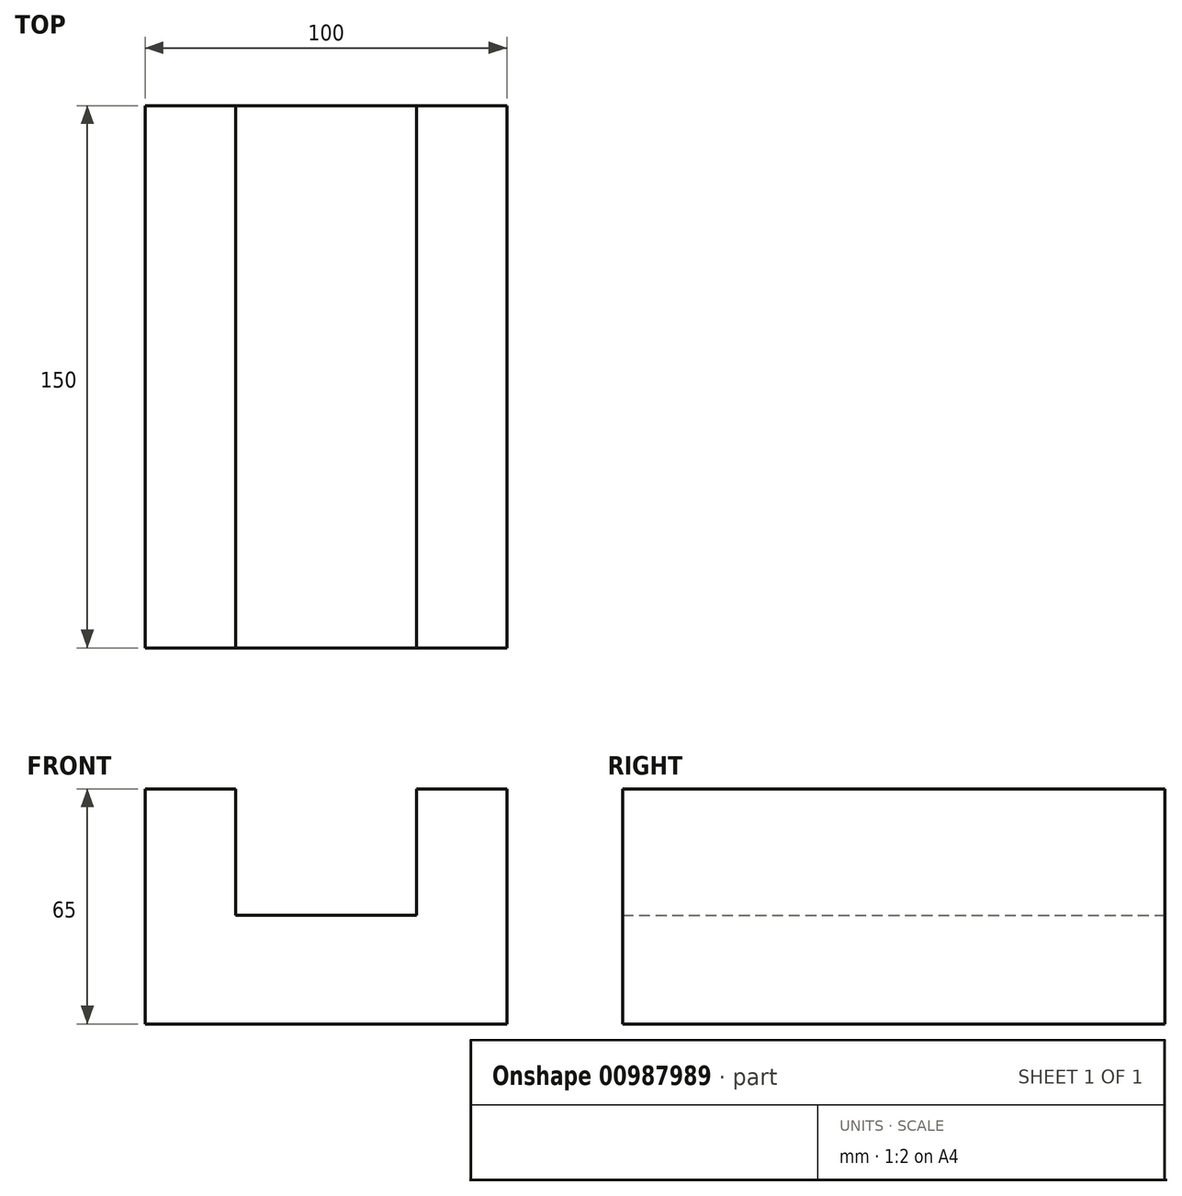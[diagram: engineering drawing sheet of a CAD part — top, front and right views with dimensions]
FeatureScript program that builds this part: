
annotation { "Feature Type Name" : "Feature", "Feature Type Description" : "" }
export const myFeature = defineFeature(function(context is Context, id is Id, definition is map)
    precondition{}
    {
        {
            var Q0;
            Q0=qCreatedBy(makeId("Front.planeOp"),FACE);
            var sketch = newSketch(context, id + "F0", { "sketchPlane" : qUnion([Q0])});
            skLineSegment(sketch, "E0", {"start": v(-50, 65) * mm, "end": v(-50, 0) * mm});
            skLineSegment(sketch, "E1", {"start": v(-50, 0) * mm, "end": v(50, 0) * mm});
            skLineSegment(sketch, "E2", {"start": v(50, 0) * mm, "end": v(50, 65) * mm});
            skLineSegment(sketch, "E3", {"start": v(50, 65) * mm, "end": v(25, 65) * mm});
            skLineSegment(sketch, "E4", {"start": v(25, 65) * mm, "end": v(25, 30) * mm});
            skLineSegment(sketch, "E5", {"start": v(25, 30) * mm, "end": v(-25, 30) * mm});
            skLineSegment(sketch, "E6", {"start": v(-25, 30) * mm, "end": v(-25, 65) * mm});
            skLineSegment(sketch, "E7", {"start": v(-25, 65) * mm, "end": v(-50, 65) * mm});
            skSolve(sketch);
        }
        {
            var Q0;
            Q0=makeQuery(id+"F0.imprint","IMPRINT",FACE,{"disambiguationData":[TD([[makeQuery(id+"F0.imprint","IMPRINT",EDGE,{"derivedFrom":sQuery(id+"F0.wireOp",EDGE,"E0")}),1.0]])]});
            extrude(context, id + "F1", {"entities" : qUnion([Q0]), "endBound" : BoundingType.SYMMETRIC, "depth" : 150 * mm, "offsetDistance" : 25 * mm});
        }
    });
